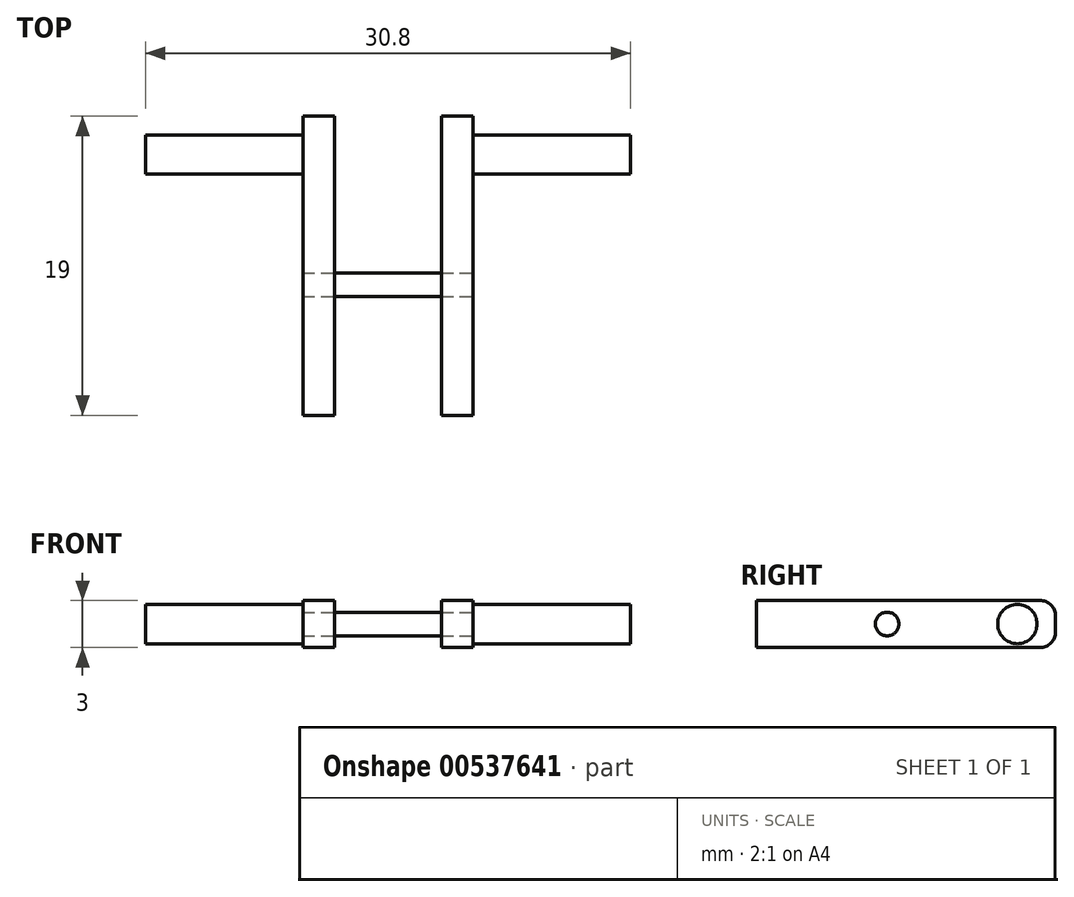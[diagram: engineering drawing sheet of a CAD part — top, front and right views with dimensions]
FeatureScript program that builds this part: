
annotation { "Feature Type Name" : "Feature", "Feature Type Description" : "" }
export const myFeature = defineFeature(function(context is Context, id is Id, definition is map)
    precondition{}
    {
        {
            var Q0;
            Q0=qCreatedBy(makeId("Right.planeOp"),FACE);
            var sketch = newSketch(context, id + "F0", { "sketchPlane" : qUnion([Q0])});
            skLineSegment(sketch, "E0.bottom", {"start": v(9.5, 1.5) * mm, "end": v(-9.5, 1.5) * mm});
            skLineSegment(sketch, "E0.top", {"start": v(9.5, -1.5) * mm, "end": v(-9.5, -1.5) * mm});
            skLineSegment(sketch, "E0.left", {"start": v(9.5, 1.5) * mm, "end": v(9.5, -1.5) * mm});
            skLineSegment(sketch, "E0.right", {"start": v(-9.5, 1.5) * mm, "end": v(-9.5, -1.5) * mm});
            skPoint(sketch, "E0.middle", {"position": v(0, 0) * mm});
            skSolve(sketch);
        }
        {
            var Q0;
            Q0=makeQuery(id+"F0.imprint","IMPRINT",FACE,{"disambiguationData":[TD([[makeQuery(id+"F0.imprint","IMPRINT",EDGE,{"derivedFrom":sQuery(id+"F0.wireOp",EDGE,"E0.bottom")}),1.0]])]});
            extrude(context, id + "F1", {"entities" : qUnion([Q0]), "depth" : 2 * mm, "offsetDistance" : 25 * mm});
        }
        {
            var Q0;
            Q0=makeQuery(id+"F1.opExtrude","CAP_FACE",FACE,{"disambiguationData":[OSD([sQuery(id+"F0.wireOp",EDGE,"E0.bottom"),sQuery(id+"F0.wireOp",EDGE,"E0.top"),sQuery(id+"F0.wireOp",EDGE,"E0.left"),sQuery(id+"F0.wireOp",EDGE,"E0.right")])],"isStart":false});
            var sketch = newSketch(context, id + "F2", { "sketchPlane" : qUnion([Q0])});
            skCircle(sketch, "E1", {"center": v(7.07, 0) * mm, "radius": 1.25 * mm});
            skSolve(sketch);
        }
        {
            var Q0;
            Q0=makeQuery(id+"F2.imprint","IMPRINT",FACE,{"disambiguationData":[TD([[makeQuery(id+"F2.imprint","IMPRINT",EDGE,{"derivedFrom":sQuery(id+"F2.wireOp",EDGE,"E1")}),1.0]])]});
            extrude(context, id + "F3", {"entities" : qUnion([Q0]), "operationType" : NewBodyOperationType.ADD, "depth" : 10 * mm, "offsetDistance" : 25 * mm});
        }
        {
            var Q0;
            Q0=makeQuery(id+"F1.opExtrude","SWEPT_EDGE",EDGE,{"disambiguationData":[OSD([sQuery(id+"F0.wireOp",EDGE,"E0.bottom"),sQuery(id+"F0.wireOp",EDGE,"E0.left")])]});
            var Q1;
            Q1=makeQuery(id+"F1.opExtrude","SWEPT_EDGE",EDGE,{"disambiguationData":[OSD([sQuery(id+"F0.wireOp",EDGE,"E0.top"),sQuery(id+"F0.wireOp",EDGE,"E0.left")])]});
            fillet(context, id + "F4", {"entities" : qUnion([Q0, Q1]), "tangentPropagation" : true, "radius" : 1 * mm, "defaultsChanged" : false, "vertexSettings" : [], "allowEdgeOverflow" : false});
        }
        {
            var Q0;
            Q0=makeQuery(id+"F1.opExtrude","SWEPT_BODY",BODY,{"disambiguationData":[OSD([sQuery(id+"F0.wireOp",EDGE,"E0.bottom"),sQuery(id+"F0.wireOp",EDGE,"E0.top"),sQuery(id+"F0.wireOp",EDGE,"E0.left"),sQuery(id+"F0.wireOp",EDGE,"E0.right")])]});
            var Q1;
            Q1=makeQuery(id+"F1.opExtrude","CAP_FACE",FACE,{"disambiguationData":[OSD([sQuery(id+"F0.wireOp",EDGE,"E0.bottom"),sQuery(id+"F0.wireOp",EDGE,"E0.top"),sQuery(id+"F0.wireOp",EDGE,"E0.left"),sQuery(id+"F0.wireOp",EDGE,"E0.right")])],"isStart":true});
            mirror(context, id + "F5", {"entities" : qUnion([Q0]), "mirrorPlane" : qUnion([Q1])});
        }
        {
            var Q0;
            Q0=makeQuery(id+"F5.opPattern","COPY",BODY,{"derivedFrom":makeQuery(id+"F1.opExtrude","SWEPT_BODY",BODY,{"disambiguationData":[OSD([sQuery(id+"F0.wireOp",EDGE,"E0.bottom"),sQuery(id+"F0.wireOp",EDGE,"E0.top"),sQuery(id+"F0.wireOp",EDGE,"E0.left"),sQuery(id+"F0.wireOp",EDGE,"E0.right")])]}),"instanceName":"1"});
            transform(context, id + "F6", {"entities" : qUnion([Q0]), "transformType" : TransformType.TRANSLATION_3D, "dx" : -6.8 * mm, "dy" : 0 * mm, "dz" : 0 * mm, "makeCopy" : false});
        }
        {
            var Q0;
            Q0=makeQuery(id+"F1.opExtrude","CAP_FACE",FACE,{"disambiguationData":[OSD([sQuery(id+"F0.wireOp",EDGE,"E0.bottom"),sQuery(id+"F0.wireOp",EDGE,"E0.top"),sQuery(id+"F0.wireOp",EDGE,"E0.left"),sQuery(id+"F0.wireOp",EDGE,"E0.right")])],"isStart":false});
            var sketch = newSketch(context, id + "F7", { "sketchPlane" : qUnion([Q0])});
            skCircle(sketch, "E2", {"center": v(-1.2, 0) * mm, "radius": 0.75 * mm});
            skSolve(sketch);
        }
        {
            var Q0;
            Q0=makeQuery(id+"F7.imprint","IMPRINT",FACE,{"disambiguationData":[TD([[makeQuery(id+"F7.imprint","IMPRINT",EDGE,{"derivedFrom":sQuery(id+"F7.wireOp",EDGE,"E2")}),1.0]])]});
            var Q1;
            Q1=makeQuery(id+"F5.opPattern","COPY",FACE,{"derivedFrom":makeQuery(id+"F1.opExtrude","CAP_FACE",FACE,{"disambiguationData":[OSD([sQuery(id+"F0.wireOp",EDGE,"E0.bottom"),sQuery(id+"F0.wireOp",EDGE,"E0.top"),sQuery(id+"F0.wireOp",EDGE,"E0.left"),sQuery(id+"F0.wireOp",EDGE,"E0.right")])],"isStart":false}),"instanceName":"1"});
            extrude(context, id + "F8", {"entities" : qUnion([Q0]), "endBound" : BoundingType.UP_TO_SURFACE, "oppositeDirection" : true, "depth" : 25 * mm, "endBoundEntityFace" : qUnion([Q1]), "offsetDistance" : 25 * mm});
        }
    });
